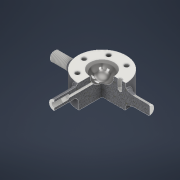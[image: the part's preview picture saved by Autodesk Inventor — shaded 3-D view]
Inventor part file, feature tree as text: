
AUTODESK INVENTOR PART (.ipt)
format: ipt  version: 2022 (Build 260153000, 153)  size: 269,824 bytes
history: native  units: mm
features: sketch x7, chamfer x4, extrude x3, other x2, revolve x2, hole x2, thread x1, mirror x1, pattern_circular x1
ambient origin geometry x8: Origin, YZ Plane, XZ Plane, XY Plane, X Axis, Y Axis, Z Axis, Center Point
bodies: Body1 (feature_tree)
feature tree (23):
  extrude  "Выдавливание8"  Depth=100.0mm
  other  "РабПлоскость16"
  revolve  "Вращение8"
  chamfer  "Фаска8"  Distance=50.0mm
  thread  "Резьба4"
  chamfer  "Фаска9"  Distance=100.0mm
  mirror  "Зеркальное отражение4"
  revolve  "Вращение9"
  other  "РабПлоскость17"
  extrude  "Выдавливание9"  Depth=10.0mm
  chamfer  "Фаска10"  Distance=35.0mm
  hole  "Отверстие6"  [1 undecoded]
  extrude  "Выдавливание10"  TaperAngle=360.0deg  [1 undecoded]
  hole  "Отверстие7"  [1 undecoded]
  pattern_circular  "Круговой массив4"  [2 undecoded]
  chamfer  "Фаска11"  Distance=2.0mm Angle=45.0deg
  sketch  "Эскиз23"
  sketch  "Эскиз25"
  sketch  "Эскиз26"
  sketch  "Эскиз29"
  sketch  "Эскиз30"
  sketch  "Эскиз31"
  sketch  "Эскиз32"
note: 5 required parameter values undecoded (feature->parameter linkage not recoverable at this tier; creation-order binding heuristic only, values carry confidence <= 0.55)
